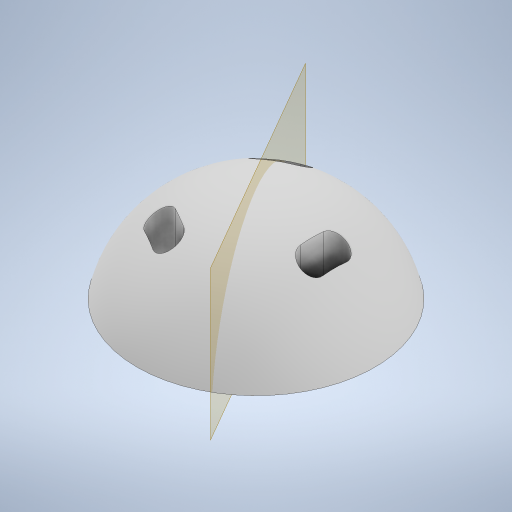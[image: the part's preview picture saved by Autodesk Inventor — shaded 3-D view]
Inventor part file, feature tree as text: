
AUTODESK INVENTOR PART (.ipt)
format: ipt  version: 2024.2 (Build 282272000, 272)  size: 321,024 bytes
history: native  units: mm
features: extrude x3, other x2, sketch x2, revolve x1
ambient origin geometry x8: Origin, YZ Plane, XZ Plane, XY Plane, X Axis, Y Axis, Z Axis, Center Point
bodies: Body1 (feature_tree)
feature tree (8):
  other  "Bryła1"
  sketch  "Szkic1"
  revolve  "Obrót1"
  extrude  "Wyciągnięcie proste1"  Depth=39.24mm
  extrude  "Wyciągnięcie proste2"  Depth=3.5mm
  extrude  "Wyciągnięcie proste3"  Depth=3.490659mm
  other  "Płaszczyzna konstrukcyjna2"
  sketch  "Szkic3"
